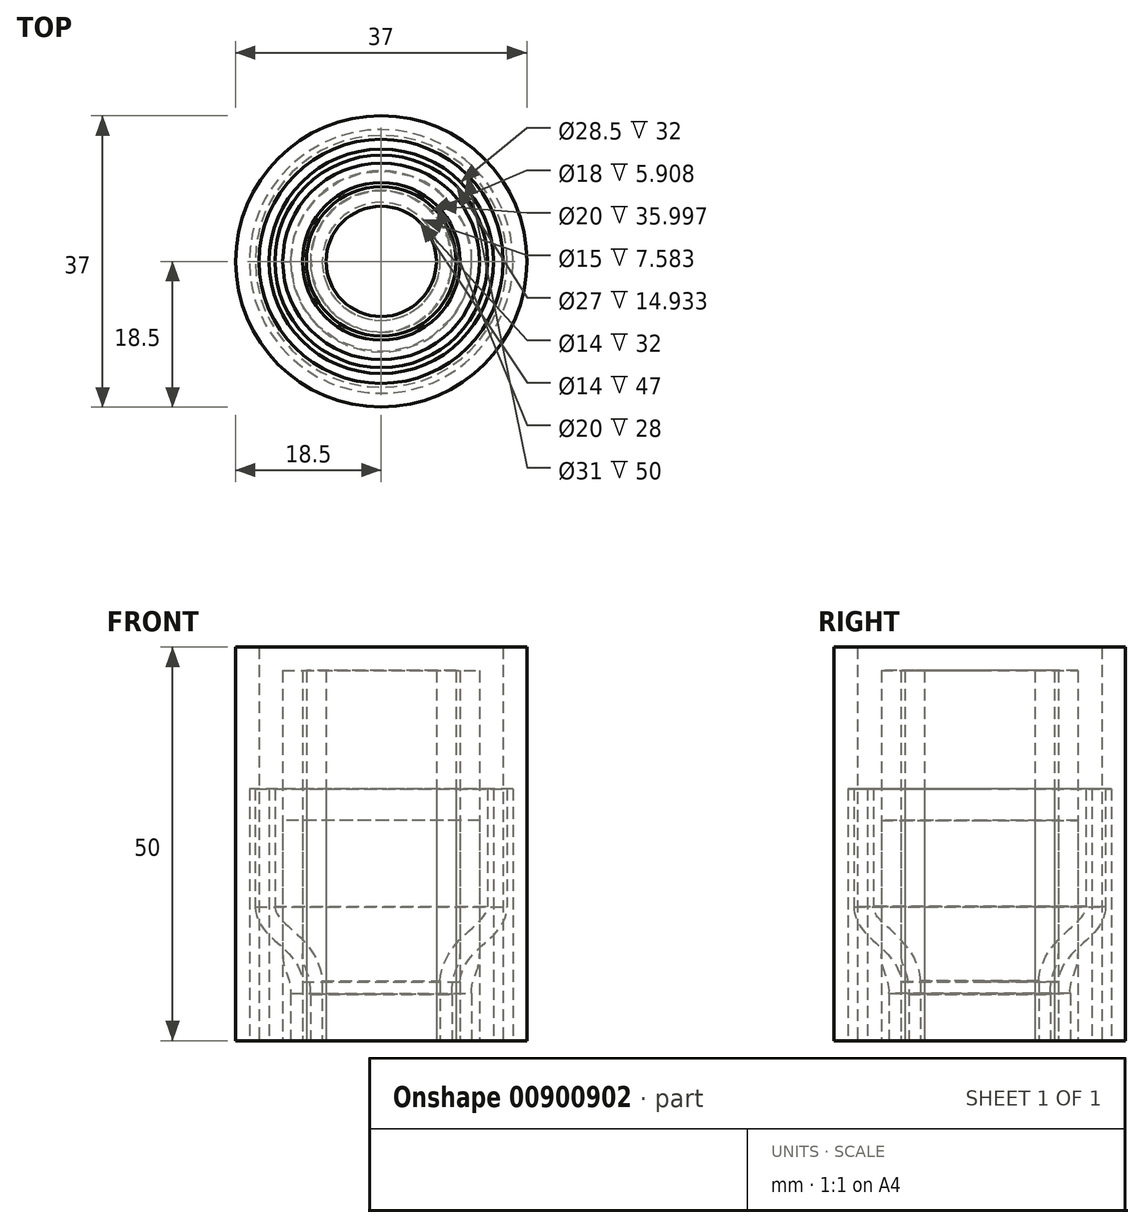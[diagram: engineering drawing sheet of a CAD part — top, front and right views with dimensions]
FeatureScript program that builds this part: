
annotation { "Feature Type Name" : "Feature", "Feature Type Description" : "" }
export const myFeature = defineFeature(function(context is Context, id is Id, definition is map)
    precondition{}
    {
        {
            var Q0;
            Q0=qCreatedBy(makeId("Right.planeOp"),FACE);
            var sketch = newSketch(context, id + "F0", { "sketchPlane" : qUnion([Q0])});
            skLineSegment(sketch, "E0", {"start": v(-11.5, 6) * mm, "end": v(-11.5, 0) * mm});
            skLineSegment(sketch, "E1", {"start": v(-11.5, 0) * mm, "end": v(0, 0) * mm});
            skLineSegment(sketch, "E2", {"start": v(0, 0) * mm, "end": v(0, 47) * mm});
            skLineSegment(sketch, "E3", {"start": v(0, 47) * mm, "end": v(-12.5, 47) * mm});
            skLineSegment(sketch, "E4", {"start": v(-12.5, 47) * mm, "end": v(-12.5, 11) * mm});
            skFitSpline(sketch, "E5", {"points": [v(-12.5, 11) * mm, v(-12, 8.5) * mm, v(-11.5, 6) * mm], "startDerivative": vector(0, -7.4) * mm, "endDerivative": vector(-0.5, -6.07) * mm});
            skSolve(sketch);
        }
        {
            var Q0;
            Q0 = qSketchRegion(id + "F0", true);
            var Q1;
            Q1=sQuery(id+"F0.wireOp",EDGE,"E2");
            revolve(context, id + "F1", {"surfaceOperationType" : NewSurfaceOperationType.NEW, "entities" : qUnion([Q0]), "axis" : qUnion([Q1]), "revolveType" : RevolveType.FULL});
        }
        {
            var Q0;
            Q0=makeQuery(id+"F1.opRevolve","SWEPT_FACE",FACE,{"disambiguationData":[OSD([sQuery(id+"F0.wireOp",EDGE,"E3")])]});
            var Q1;
            Q1=makeQuery(id+"F1.opRevolve","SWEPT_FACE",FACE,{"disambiguationData":[OSD([sQuery(id+"F0.wireOp",EDGE,"E1")])]});
            shell(context, id + "F2", {"entities" : qUnion([Q0, Q1]), "thickness" : 2.5 * mm});
        }
        {
            var Q0;
            Q0=qCreatedBy(makeId("Top.planeOp"),FACE);
            var sketch = newSketch(context, id + "F3", { "sketchPlane" : qUnion([Q0])});
            skCircle(sketch, "E6", {"center": v(0, 0) * mm, "radius": 14.25 * mm});
            skCircle(sketch, "E7", {"center": v(0, 0) * mm, "radius": 16.75 * mm});
            skSolve(sketch);
        }
        {
            var Q0;
            Q0 = qSketchRegion(id + "F3", true);
            extrude(context, id + "F4", {"entities" : qUnion([Q0]), "depth" : 32 * mm, "offsetDistance" : 25 * mm});
        }
        {
            var Q0;
            Q0=qCreatedBy(makeId("Top.planeOp"),FACE);
            var sketch = newSketch(context, id + "F5", { "sketchPlane" : qUnion([Q0])});
            skCircle(sketch, "E8", {"center": v(0, 0) * mm, "radius": 18.5 * mm});
            skCircle(sketch, "E9", {"center": v(0, 0) * mm, "radius": 15.5 * mm});
            skSolve(sketch);
        }
        {
            var Q0;
            Q0 = qSketchRegion(id + "F5", true);
            extrude(context, id + "F6", {"entities" : qUnion([Q0]), "depth" : 50 * mm, "offsetDistance" : 25 * mm});
        }
        {
            var Q0;
            Q0=qCreatedBy(makeId("Top.planeOp"),FACE);
            var sketch = newSketch(context, id + "F7", { "sketchPlane" : qUnion([Q0])});
            skCircle(sketch, "E10", {"center": v(0, 0) * mm, "radius": 7 * mm});
            skCircle(sketch, "E11", {"center": v(0, 0) * mm, "radius": 9.5 * mm});
            skSolve(sketch);
        }
        {
            var Q0;
            Q0 = qSketchRegion(id + "F7", true);
            extrude(context, id + "F8", {"entities" : qUnion([Q0]), "depth" : 47 * mm, "offsetDistance" : 25 * mm});
        }
        {
            var Q0;
            Q0=qCreatedBy(makeId("Top.planeOp"),FACE);
            var sketch = newSketch(context, id + "F9", { "sketchPlane" : qUnion([Q0])});
            skCircle(sketch, "E12", {"center": v(0, 0) * mm, "radius": 7 * mm});
            skCircle(sketch, "E13", {"center": v(0, 0) * mm, "radius": 9.5 * mm});
            skSolve(sketch);
        }
        {
            var Q0;
            Q0 = qSketchRegion(id + "F9", true);
            extrude(context, id + "F10", {"entities" : qUnion([Q0]), "depth" : 32 * mm, "offsetDistance" : 25 * mm});
        }
        {
            var Q0;
            Q0=qCreatedBy(makeId("Right.planeOp"),FACE);
            var sketch = newSketch(context, id + "F11", { "sketchPlane" : qUnion([Q0])});
            skLineSegment(sketch, "E14", {"start": v(-10, 0) * mm, "end": v(0, 0) * mm});
            skLineSegment(sketch, "E15", {"start": v(0, 0) * mm, "end": v(0, 32) * mm});
            skLineSegment(sketch, "E16", {"start": v(0, 32) * mm, "end": v(-16, 32) * mm});
            skLineSegment(sketch, "E17", {"start": v(-16, 32) * mm, "end": v(-16, 17) * mm});
            skLineSegment(sketch, "E18", {"start": v(-10, 0) * mm, "end": v(-10, 7.5) * mm});
            skFitSpline(sketch, "E19", {"points": [v(-16, 17) * mm, v(-13, 12.25) * mm, v(-10, 7.5) * mm], "startDerivative": vector(0.63, -13.55) * mm, "endDerivative": vector(0.82, -12.31) * mm});
            skSolve(sketch);
        }
        {
            var Q0;
            Q0 = qSketchRegion(id + "F11", true);
            var Q1;
            Q1=sQuery(id+"F11.wireOp",EDGE,"E15");
            revolve(context, id + "F12", {"surfaceOperationType" : NewSurfaceOperationType.NEW, "entities" : qUnion([Q0]), "axis" : qUnion([Q1]), "revolveType" : RevolveType.FULL});
        }
        {
            var Q0;
            Q0=makeQuery(id+"F12.opRevolve","SWEPT_FACE",FACE,{"disambiguationData":[OSD([sQuery(id+"F11.wireOp",EDGE,"E16")])]});
            var Q1;
            Q1=makeQuery(id+"F12.opRevolve","SWEPT_FACE",FACE,{"disambiguationData":[OSD([sQuery(id+"F11.wireOp",EDGE,"E14")])]});
            shell(context, id + "F13", {"entities" : qUnion([Q0, Q1]), "thickness" : 2.5 * mm});
        }
        {
            var Q0;
            Q0=qCreatedBy(makeId("Top.planeOp"),FACE);
            var sketch = newSketch(context, id + "F14", { "sketchPlane" : qUnion([Q0])});
            skCircle(sketch, "E20", {"center": v(0, 0) * mm, "radius": 10 * mm});
            skCircle(sketch, "E21", {"center": v(0, 0) * mm, "radius": 12.5 * mm});
            skSolve(sketch);
        }
        {
            var Q0;
            Q0 = qSketchRegion(id + "F14", true);
            extrude(context, id + "F15", {"entities" : qUnion([Q0]), "depth" : 28 * mm, "offsetDistance" : 25 * mm});
        }
    });
